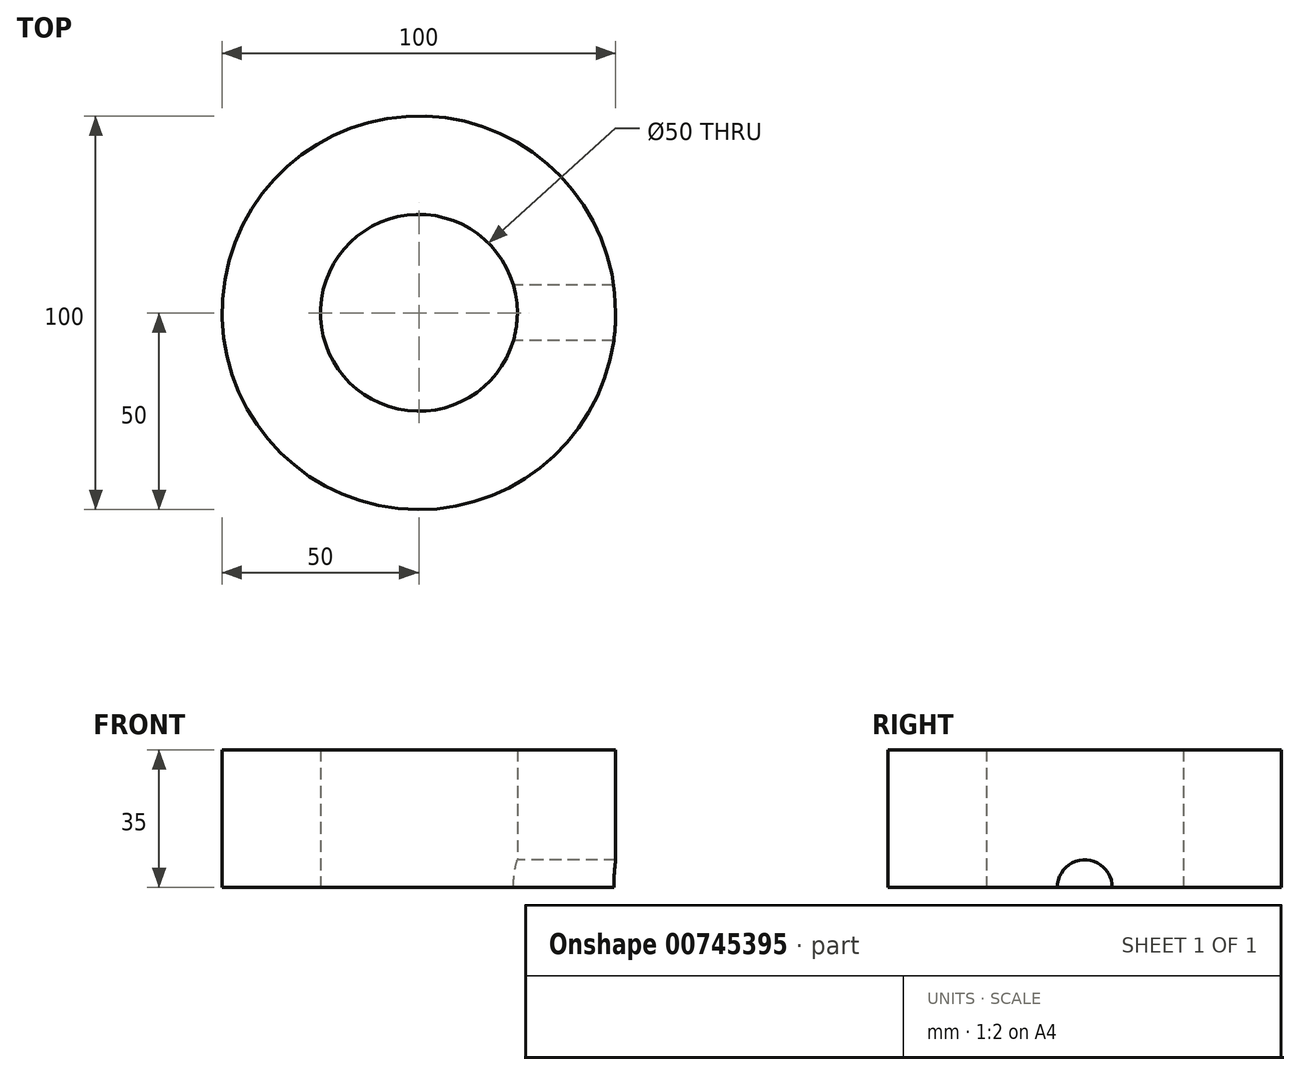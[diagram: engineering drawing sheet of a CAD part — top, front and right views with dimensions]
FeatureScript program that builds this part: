
annotation { "Feature Type Name" : "Feature", "Feature Type Description" : "" }
export const myFeature = defineFeature(function(context is Context, id is Id, definition is map)
    precondition{}
    {
        {
            var Q0;
            Q0=qCreatedBy(makeId("Top.planeOp"),FACE);
            var sketch = newSketch(context, id + "F0", { "sketchPlane" : qUnion([Q0])});
            skCircle(sketch, "E0", {"center": v(0, 0) * mm, "radius": 50 * mm});
            skSolve(sketch);
        }
        {
            var Q0;
            Q0 = qSketchRegion(id + "F0", true);
            extrude(context, id + "F1", {"entities" : qUnion([Q0]), "depth" : 35 * mm, "offsetDistance" : 25 * mm});
        }
        {
            var Q0;
            Q0=qCreatedBy(makeId("Top.planeOp"),FACE);
            var sketch = newSketch(context, id + "F2", { "sketchPlane" : qUnion([Q0])});
            skCircle(sketch, "E1", {"center": v(0, 0) * mm, "radius": 25 * mm});
            skSolve(sketch);
        }
        {
            var Q0;
            Q0 = qSketchRegion(id + "F2", true);
            extrude(context, id + "F3", {"entities" : qUnion([Q0]), "operationType" : NewBodyOperationType.REMOVE, "depth" : 35 * mm, "offsetDistance" : 25 * mm});
        }
        {
            var Q0;
            Q0=qCreatedBy(makeId("Right.planeOp"),FACE);
            var sketch = newSketch(context, id + "F4", { "sketchPlane" : qUnion([Q0])});
            skCircle(sketch, "E2", {"center": v(0, 0) * mm, "radius": 7 * mm});
            skSolve(sketch);
        }
        {
            var Q0;
            Q0 = qSketchRegion(id + "F4", true);
            extrude(context, id + "F5", {"entities" : qUnion([Q0]), "operationType" : NewBodyOperationType.REMOVE, "endBound" : BoundingType.THROUGH_ALL, "depth" : 25 * mm, "offsetDistance" : 25 * mm});
        }
    });
